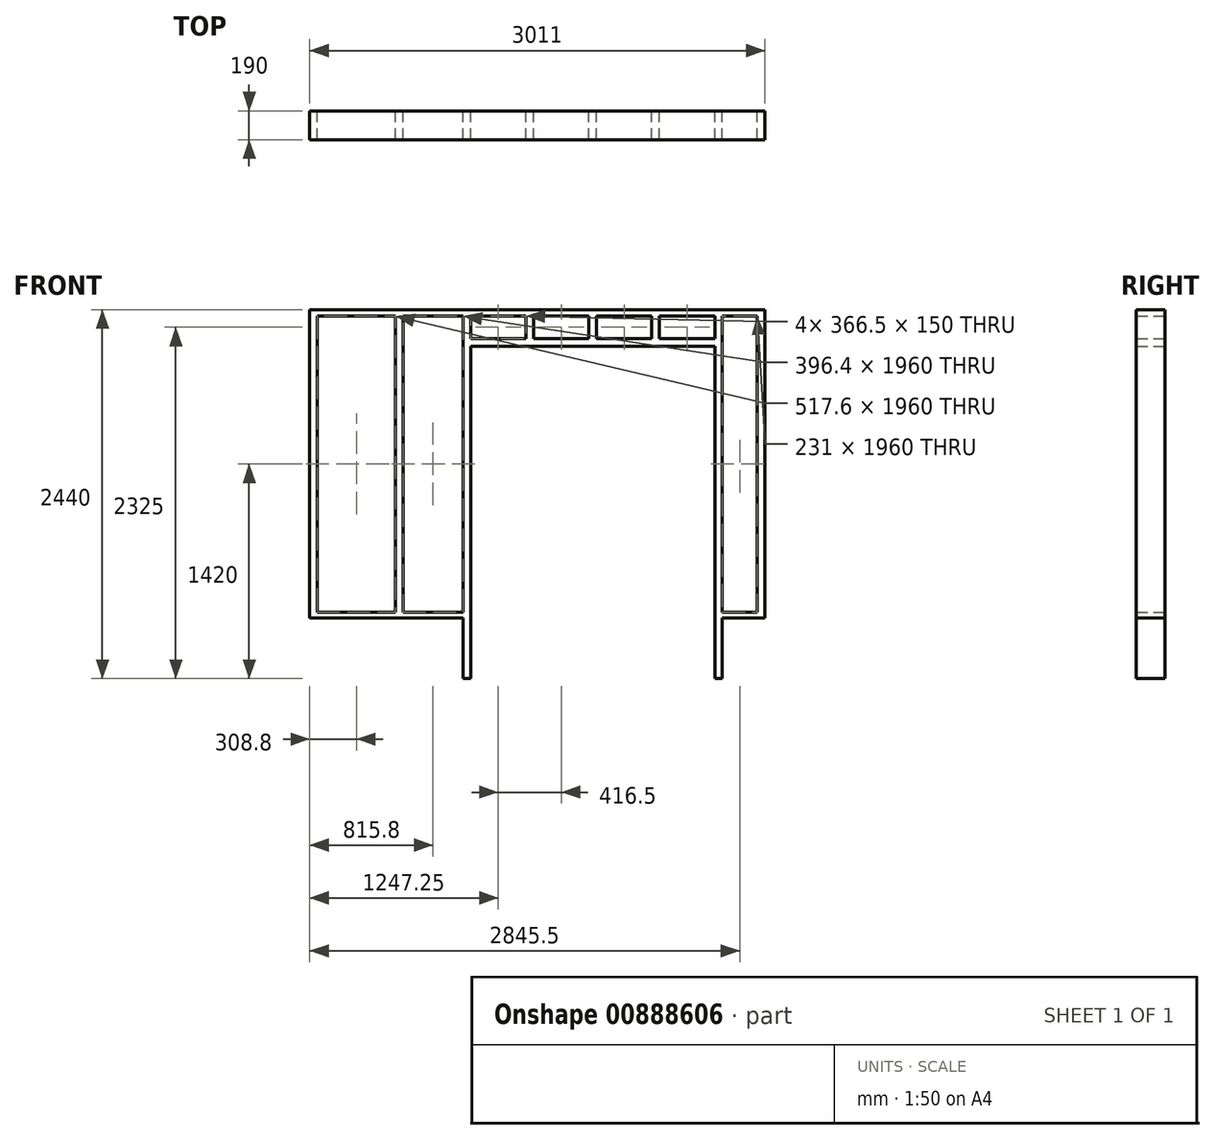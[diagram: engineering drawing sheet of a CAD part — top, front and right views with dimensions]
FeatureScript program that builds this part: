
annotation { "Feature Type Name" : "Feature", "Feature Type Description" : "" }
export const myFeature = defineFeature(function(context is Context, id is Id, definition is map)
    precondition{}
    {
        {
            var Q0;
            Q0=qCreatedBy(makeId("Front.planeOp"),FACE);
            var sketch = newSketch(context, id + "F0", { "sketchPlane" : qUnion([Q0])});
            skLineSegment(sketch, "E0.bottom", {"start": v(-1505.5, 0) * mm, "end": v(0, 0) * mm});
            skLineSegment(sketch, "E0.top", {"start": v(-1505.5, 40) * mm, "end": v(-491.5, 40) * mm});
            skLineSegment(sketch, "E0.left", {"start": v(-1505.5, 0) * mm, "end": v(-1505.5, 40) * mm});
            skLineSegment(sketch, "E0.right", {"start": v(1505.5, 0) * mm, "end": v(1505.5, 40) * mm});
            skPoint(sketch, "E1", {"position": v(0, 0) * mm});
            skLineSegment(sketch, "E2.bottom", {"start": v(1505.5, 2040) * mm, "end": v(-1505.5, 2040) * mm});
            skLineSegment(sketch, "E2.top", {"start": v(1505.5, 2000) * mm, "end": v(-1505.5, 2000) * mm});
            skLineSegment(sketch, "E2.left", {"start": v(1505.5, 2040) * mm, "end": v(1505.5, 2000) * mm});
            skLineSegment(sketch, "E2.right", {"start": v(-1505.5, 2040) * mm, "end": v(-1505.5, 2000) * mm});
            skLineSegment(sketch, "E3", {"start": v(1224.5, 40) * mm, "end": v(1224.5, 0) * mm});
            skLineSegment(sketch, "E4", {"start": v(-491.5, 0) * mm, "end": v(-491.5, 40) * mm});
            skLineSegment(sketch, "E5.trimOffspring", {"start": v(1224.5, 40) * mm, "end": v(1505.5, 40) * mm});
            skLineSegment(sketch, "E6.trimOffspring", {"start": v(1224.5, 0) * mm, "end": v(1505.5, 0) * mm});
            skSolve(sketch);
        }
        {
            var Q0;
            Q0=makeQuery(id+"F0.imprint","IMPRINT",FACE,{"disambiguationData":[TD([[makeQuery(id+"F0.imprint","IMPRINT",EDGE,{"derivedFrom":sQuery(id+"F0.wireOp",EDGE,"E0.bottom")}),1.0]])]});
            extrude(context, id + "F1", {"entities" : qUnion([Q0]), "depth" : 190 * mm, "offsetDistance" : 25 * mm});
        }
        {
            var Q0;
            Q0=makeQuery(id+"F0.imprint","IMPRINT",FACE,{"disambiguationData":[TD([[makeQuery(id+"F0.imprint","IMPRINT",EDGE,{"derivedFrom":sQuery(id+"F0.wireOp",EDGE,"E2.bottom")}),1.0]])]});
            extrude(context, id + "F2", {"entities" : qUnion([Q0]), "depth" : 190 * mm, "offsetDistance" : 25 * mm});
        }
        {
            var Q0;
            Q0=qCreatedBy(makeId("Front.planeOp"),FACE);
            var sketch = newSketch(context, id + "F3", { "sketchPlane" : qUnion([Q0])});
            skLineSegment(sketch, "E7.bottom", {"start": v(1505.5, 2000) * mm, "end": v(1455.5, 2000) * mm});
            skLineSegment(sketch, "E7.top", {"start": v(1505.5, 40) * mm, "end": v(1455.5, 40) * mm});
            skLineSegment(sketch, "E7.left", {"start": v(1505.5, 2000) * mm, "end": v(1505.5, 40) * mm});
            skLineSegment(sketch, "E7.right", {"start": v(1455.5, 2000) * mm, "end": v(1455.5, 40) * mm});
            skLineSegment(sketch, "E8.1.0.0", {"start": v(1174.5, 2000) * mm, "end": v(1174.5, -400) * mm});
            skLineSegment(sketch, "E8.1.0.1", {"start": v(1224.5, 2000) * mm, "end": v(1224.5, -400) * mm});
            skLineSegment(sketch, "E8.1.0.2", {"start": v(1224.5, 2000) * mm, "end": v(1174.5, 2000) * mm});
            skLineSegment(sketch, "E8.2.0.0", {"start": v(758, 2000) * mm, "end": v(758, 1850) * mm});
            skLineSegment(sketch, "E8.2.0.1", {"start": v(808, 2000) * mm, "end": v(808, 1850) * mm});
            skLineSegment(sketch, "E8.2.0.2", {"start": v(808, 2000) * mm, "end": v(758, 2000) * mm});
            skLineSegment(sketch, "E8.2.0.3", {"start": v(808, 1850) * mm, "end": v(758, 1850) * mm});
            skLineSegment(sketch, "E8.3.0.0", {"start": v(341.5, 2000) * mm, "end": v(341.5, 1850) * mm});
            skLineSegment(sketch, "E8.3.0.1", {"start": v(391.5, 2000) * mm, "end": v(391.5, 1850) * mm});
            skLineSegment(sketch, "E8.3.0.2", {"start": v(391.5, 2000) * mm, "end": v(341.5, 2000) * mm});
            skLineSegment(sketch, "E8.3.0.3", {"start": v(391.5, 1850) * mm, "end": v(341.5, 1850) * mm});
            skLineSegment(sketch, "E8.4.0.0", {"start": v(-75, 2000) * mm, "end": v(-75, 1850) * mm});
            skLineSegment(sketch, "E8.4.0.1", {"start": v(-25, 2000) * mm, "end": v(-25, 1850) * mm});
            skLineSegment(sketch, "E8.4.0.2", {"start": v(-25, 2000) * mm, "end": v(-75, 2000) * mm});
            skLineSegment(sketch, "E8.4.0.3", {"start": v(-25, 1850) * mm, "end": v(-75, 1850) * mm});
            skLineSegment(sketch, "E8.5.0.0", {"start": v(-491.5, 2000) * mm, "end": v(-491.5, -400) * mm});
            skLineSegment(sketch, "E8.5.0.1", {"start": v(-441.5, 2000) * mm, "end": v(-441.5, -400) * mm});
            skLineSegment(sketch, "E8.5.0.2", {"start": v(-441.5, 2000) * mm, "end": v(-491.5, 2000) * mm});
            skLineSegment(sketch, "E8.6.0.0", {"start": v(-937.9, 2000) * mm, "end": v(-937.9, 40) * mm});
            skLineSegment(sketch, "E8.6.0.1", {"start": v(-887.9, 2000) * mm, "end": v(-887.9, 40) * mm});
            skLineSegment(sketch, "E8.6.0.2", {"start": v(-887.9, 2000) * mm, "end": v(-937.9, 2000) * mm});
            skLineSegment(sketch, "E8.6.0.3", {"start": v(-887.9, 40) * mm, "end": v(-937.9, 40) * mm});
            skLineSegment(sketch, "E8.7.0.0", {"start": v(-1505.5, 2000) * mm, "end": v(-1505.5, 40) * mm});
            skLineSegment(sketch, "E8.7.0.1", {"start": v(-1455.5, 2000) * mm, "end": v(-1455.5, 40) * mm});
            skLineSegment(sketch, "E8.7.0.2", {"start": v(-1455.5, 2000) * mm, "end": v(-1505.5, 2000) * mm});
            skLineSegment(sketch, "E8.7.0.3", {"start": v(-1455.5, 40) * mm, "end": v(-1505.5, 40) * mm});
            skLineSegment(sketch, "E9.bottom", {"start": v(1174.5, 1850) * mm, "end": v(-441.5, 1850) * mm});
            skLineSegment(sketch, "E9.top", {"start": v(1174.5, 1800) * mm, "end": v(-441.5, 1800) * mm});
            skLineSegment(sketch, "E9.left", {"start": v(1174.5, 1850) * mm, "end": v(1174.5, 1800) * mm});
            skLineSegment(sketch, "E9.right", {"start": v(-441.5, 1850) * mm, "end": v(-441.5, 1800) * mm});
            skLineSegment(sketch, "E10", {"start": v(1224.5, -400) * mm, "end": v(1174.5, -400) * mm});
            skLineSegment(sketch, "E11", {"start": v(-441.5, -400) * mm, "end": v(-491.5, -400) * mm});
            skLineSegment(sketch, "E12", {"start": v(1174.5, 1925) * mm, "end": v(808, 1925) * mm, "construction": true});
            skLineSegment(sketch, "E13", {"start": v(758, 1925) * mm, "end": v(391.5, 1925) * mm, "construction": true});
            skLineSegment(sketch, "E14", {"start": v(341.5, 1925) * mm, "end": v(-25, 1925) * mm, "construction": true});
            skPoint(sketch, "E15.endSnap0", {"position": v(-75, 1925) * mm});
            skLineSegment(sketch, "E16", {"start": v(-75, 1925) * mm, "end": v(-441.5, 1925) * mm, "construction": true});
            skSolve(sketch);
        }
        {
            var Q0;
            Q0=makeQuery(id+"F3.imprint","IMPRINT",FACE,{"disambiguationData":[TD([[makeQuery(id+"F3.imprint","IMPRINT",EDGE,{"derivedFrom":sQuery(id+"F3.wireOp",EDGE,"E7.bottom")}),1.0]])]});
            var Q1;
            Q1=makeQuery(id+"F3.imprint","IMPRINT",FACE,{"disambiguationData":[TD([[makeQuery(id+"F3.imprint","IMPRINT",EDGE,{"derivedFrom":sQuery(id+"F3.wireOp",EDGE,"E8.1.0.0")}),1.0]])]});
            var Q2;
            Q2=makeQuery(id+"F3.imprint","IMPRINT",FACE,{"disambiguationData":[TD([[makeQuery(id+"F3.imprint","IMPRINT",EDGE,{"derivedFrom":sQuery(id+"F3.wireOp",EDGE,"E8.2.0.0")}),1.0]])]});
            var Q3;
            Q3=makeQuery(id+"F3.imprint","IMPRINT",FACE,{"disambiguationData":[TD([[makeQuery(id+"F3.imprint","IMPRINT",EDGE,{"derivedFrom":sQuery(id+"F3.wireOp",EDGE,"E8.3.0.0")}),1.0]])]});
            var Q4;
            Q4=makeQuery(id+"F3.imprint","IMPRINT",FACE,{"disambiguationData":[TD([[makeQuery(id+"F3.imprint","IMPRINT",EDGE,{"derivedFrom":sQuery(id+"F3.wireOp",EDGE,"E8.4.0.0")}),1.0]])]});
            var Q5;
            Q5=makeQuery(id+"F3.imprint","IMPRINT",FACE,{"disambiguationData":[TD([[makeQuery(id+"F3.imprint","IMPRINT",EDGE,{"derivedFrom":sQuery(id+"F3.wireOp",EDGE,"E8.5.0.0")}),1.0]])]});
            var Q6;
            Q6=makeQuery(id+"F3.imprint","IMPRINT",FACE,{"disambiguationData":[TD([[makeQuery(id+"F3.imprint","IMPRINT",EDGE,{"derivedFrom":sQuery(id+"F3.wireOp",EDGE,"E8.6.0.0")}),1.0]])]});
            var Q7;
            Q7=makeQuery(id+"F3.imprint","IMPRINT",FACE,{"disambiguationData":[TD([[makeQuery(id+"F3.imprint","IMPRINT",EDGE,{"derivedFrom":sQuery(id+"F3.wireOp",EDGE,"E8.7.0.0")}),1.0]])]});
            var Q8;
            Q8=makeQuery(id+"F3.imprint","IMPRINT",FACE,{"disambiguationData":[TD([[makeQuery(id+"F3.imprint","IMPRINT",EDGE,{"derivedFrom":sQuery(id+"F3.wireOp",EDGE,"E8.8.0.0")}),1.0]])]});
            var Q9;
            Q9=makeQuery(id+"F3.imprint","IMPRINT",FACE,{"disambiguationData":[TD([[makeQuery(id+"F3.imprint","IMPRINT",EDGE,{"derivedFrom":sQuery(id+"F3.wireOp",EDGE,"E8.9.0.0")}),1.0]])]});
            var Q10;
            Q10=makeQuery(id+"F3.imprint","IMPRINT",FACE,{"disambiguationData":[TD([[makeQuery(id+"F3.imprint","IMPRINT",EDGE,{"derivedFrom":sQuery(id+"F3.wireOp",EDGE,"E9.top")}),-1.0]])]});
            var Q11;
            Q11=makeQuery(id+"F0.imprint","IMPRINT",FACE,{"disambiguationData":[TD([[makeQuery(id+"F0.imprint","IMPRINT",EDGE,{"derivedFrom":sQuery(id+"F0.wireOp",EDGE,"E0.right")}),1.0]])]});
            extrude(context, id + "F4", {"entities" : qUnion([Q0, Q1, Q2, Q3, Q4, Q5, Q6, Q7, Q8, Q9, Q10, Q11]), "operationType" : NewBodyOperationType.ADD, "depth" : 190 * mm, "offsetDistance" : 25 * mm});
        }
    });
